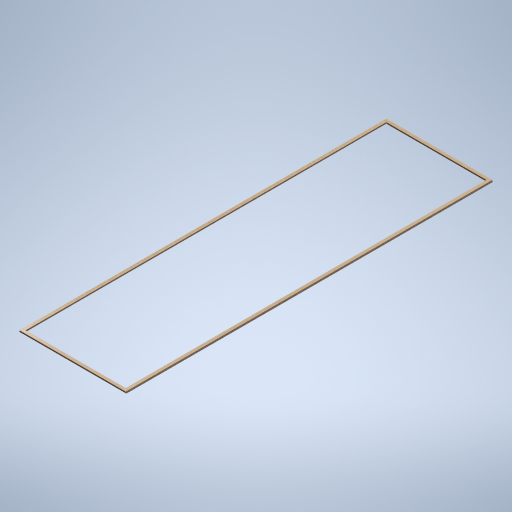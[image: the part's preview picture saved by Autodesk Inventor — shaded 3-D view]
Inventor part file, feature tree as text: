
AUTODESK INVENTOR PART (.ipt)
format: ipt  version: 2024.2 (Build 282272000, 272)  size: 282,112 bytes
history: native  units: mm
features: extrude x2, sketch x2, projected_geometry x1
ambient origin geometry x8: Origin, YZ Plane, XZ Plane, XY Plane, X Axis, Y Axis, Z Axis, Center Point
bodies: Solid1 (feature_tree)
feature tree (5):
  extrude  "Extrusion1"  Depth=8834.0mm
  extrude  "Extrusion4"  TaperAngle=0.0deg  [1 undecoded]
  sketch  "Sketch1"  dims[d1=32302.0mm d2=0.0mm d11=8834.0mm]
  sketch  "Sketch2"  dims[d12=31802.0mm d13=0.0mm d14=0.0mm]
  projected_geometry  "Projected Loop1"
note: 1 required parameter value undecoded (feature->parameter linkage not recoverable at this tier; creation-order binding heuristic only, values carry confidence <= 0.55)
